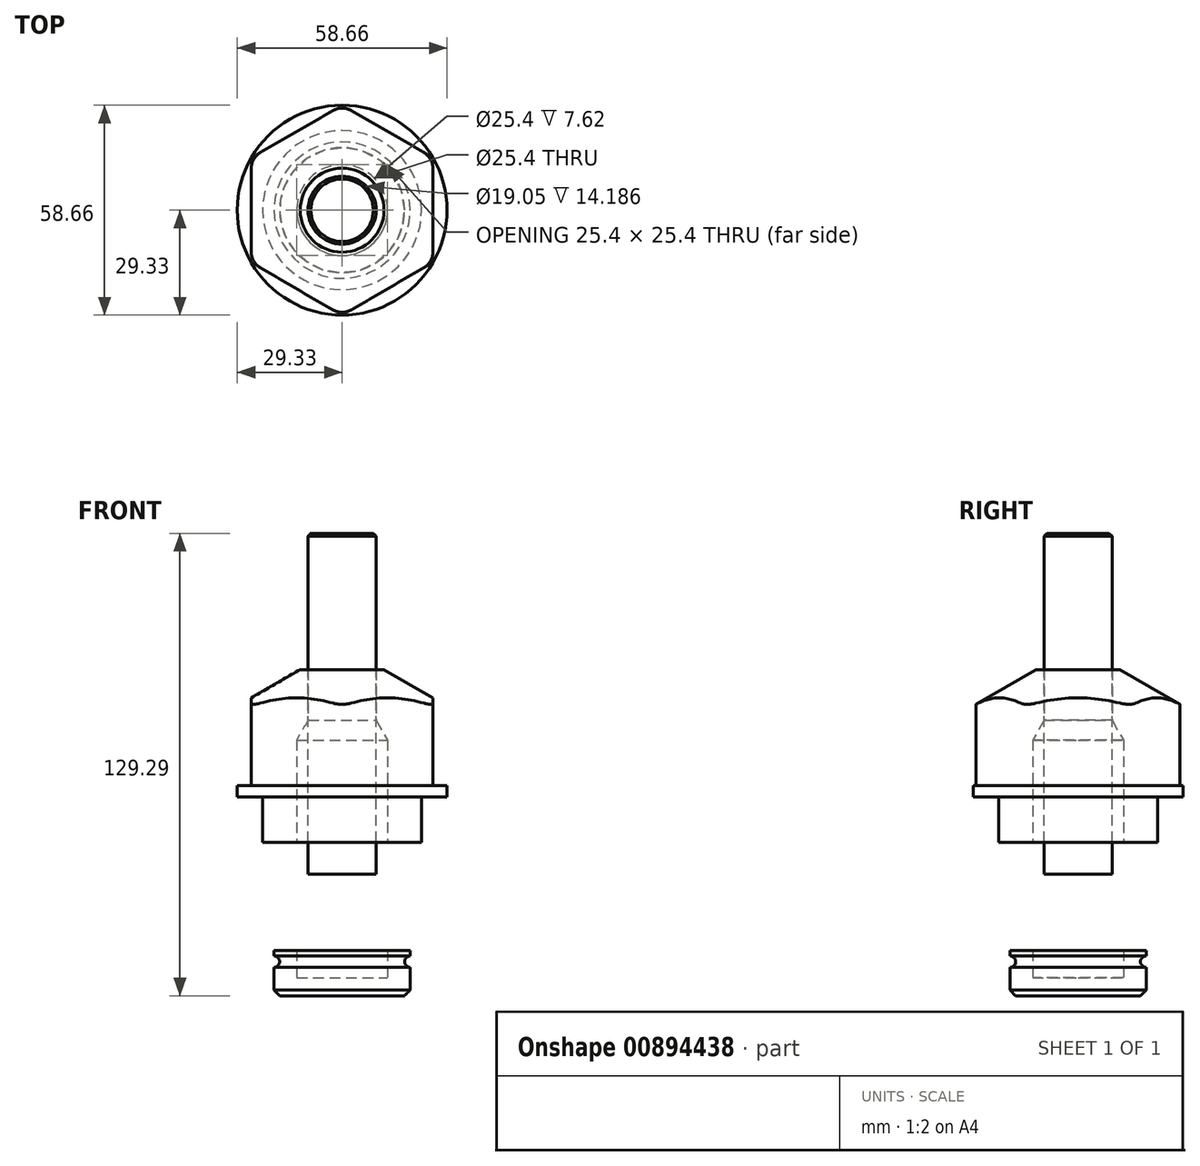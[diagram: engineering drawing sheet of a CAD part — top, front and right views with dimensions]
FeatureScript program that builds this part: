
annotation { "Feature Type Name" : "Feature", "Feature Type Description" : "" }
export const myFeature = defineFeature(function(context is Context, id is Id, definition is map)
    precondition{}
    {
        {
            var Q0;
            Q0=qCreatedBy(makeId("Top.planeOp"),FACE);
            var sketch = newSketch(context, id + "F0", { "sketchPlane" : qUnion([Q0])});
            skCircle(sketch, "E0", {"center": v(0, 0) * mm, "radius": 29.33 * mm});
            skLineSegment(sketch, "E1", {"start": v(0, 29.33) * mm, "end": v(0, -29.33) * mm, "construction": true});
            skLineSegment(sketch, "E2", {"start": v(-25.4, 14.66) * mm, "end": v(25.4, -14.66) * mm, "construction": true});
            skLineSegment(sketch, "E3", {"start": v(-25.4, -14.66) * mm, "end": v(25.4, 14.66) * mm, "construction": true});
            skLineSegment(sketch, "E4", {"start": v(-25.4, 14.66) * mm, "end": v(0, 29.33) * mm});
            skLineSegment(sketch, "E5", {"start": v(0, 29.33) * mm, "end": v(25.4, 14.66) * mm});
            skLineSegment(sketch, "E6", {"start": v(25.4, 14.66) * mm, "end": v(25.4, -14.66) * mm});
            skLineSegment(sketch, "E7", {"start": v(25.4, -14.66) * mm, "end": v(0, -29.33) * mm});
            skLineSegment(sketch, "E8", {"start": v(0, -29.33) * mm, "end": v(-25.4, -14.66) * mm});
            skLineSegment(sketch, "E9", {"start": v(-25.4, -14.66) * mm, "end": v(-25.4, 14.66) * mm});
            skCircle(sketch, "E10", {"center": v(0, 0) * mm, "radius": 7.94 * mm});
            skSolve(sketch);
        }
        {
            var Q0;
            Q0=makeQuery(id+"F0.imprint","IMPRINT",FACE,{"disambiguationData":[TD([[makeQuery(id+"F0.imprint","IMPRINT",EDGE,{"derivedFrom":sQuery(id+"F0.wireOp",EDGE,"E10")}),1.0]])]});
            var Q1;
            Q1=makeQuery(id+"F0.imprint","IMPRINT",FACE,{"disambiguationData":[TD([[makeQuery(id+"F0.imprint","IMPRINT",EDGE,{"derivedFrom":sQuery(id+"F0.wireOp",EDGE,"E4")}),-1.0]])]});
            extrude(context, id + "F1", {"entities" : qUnion([Q0, Q1]), "depth" : 35.56 * mm});
        }
        {
            var Q0;
            {var subQ0=sQuery(id+"F0.wireOp",EDGE,"E8");Q0=makeQuery(id+"F0.imprint","IMPRINT",FACE,{"disambiguationData":[TD([[makeQuery(id+"F0.imprint","IMPRINT",EDGE,{"derivedFrom":subQ0}),1.0]])]});}
            var Q1;
            {var subQ0=sQuery(id+"F0.wireOp",EDGE,"E7");Q1=makeQuery(id+"F0.imprint","IMPRINT",FACE,{"disambiguationData":[TD([[makeQuery(id+"F0.imprint","IMPRINT",EDGE,{"derivedFrom":subQ0}),1.0]])]});}
            var Q2;
            {var subQ0=sQuery(id+"F0.wireOp",EDGE,"E6");Q2=makeQuery(id+"F0.imprint","IMPRINT",FACE,{"disambiguationData":[TD([[makeQuery(id+"F0.imprint","IMPRINT",EDGE,{"derivedFrom":subQ0}),1.0]])]});}
            var Q3;
            Q3=makeQuery(id+"F0.imprint","IMPRINT",FACE,{"disambiguationData":[TD([[makeQuery(id+"F0.imprint","IMPRINT",EDGE,{"derivedFrom":sQuery(id+"F0.wireOp",EDGE,"E4")}),-1.0]])]});
            var Q4;
            {var subQ0=sQuery(id+"F0.wireOp",EDGE,"E5");Q4=makeQuery(id+"F0.imprint","IMPRINT",FACE,{"disambiguationData":[TD([[makeQuery(id+"F0.imprint","IMPRINT",EDGE,{"derivedFrom":subQ0}),1.0]])]});}
            var Q5;
            {var subQ0=sQuery(id+"F0.wireOp",EDGE,"E4");Q5=makeQuery(id+"F0.imprint","IMPRINT",FACE,{"disambiguationData":[TD([[makeQuery(id+"F0.imprint","IMPRINT",EDGE,{"derivedFrom":subQ0}),1.0]])]});}
            var Q6;
            {var subQ0=sQuery(id+"F0.wireOp",EDGE,"E9");Q6=makeQuery(id+"F0.imprint","IMPRINT",FACE,{"disambiguationData":[TD([[makeQuery(id+"F0.imprint","IMPRINT",EDGE,{"derivedFrom":subQ0}),1.0]])]});}
            extrude(context, id + "F2", {"entities" : qUnion([Q0, Q1, Q2, Q3, Q4, Q5, Q6]), "operationType" : NewBodyOperationType.ADD, "depth" : 3.17 * mm});
        }
        {
            var Q0;
            Q0=makeQuery(id+"F1.opExtrude","SWEPT_EDGE",EDGE,{"disambiguationData":[OSD([sQuery(id+"F0.wireOp",EDGE,"E0"),sQuery(id+"F0.wireOp",EDGE,"E7"),sQuery(id+"F0.wireOp",EDGE,"E8")])]});
            var Q1;
            Q1=makeQuery(id+"F1.opExtrude","SWEPT_EDGE",EDGE,{"disambiguationData":[OSD([sQuery(id+"F0.wireOp",EDGE,"E0"),sQuery(id+"F0.wireOp",EDGE,"E6"),sQuery(id+"F0.wireOp",EDGE,"E7")])]});
            var Q2;
            Q2=makeQuery(id+"F1.opExtrude","SWEPT_EDGE",EDGE,{"disambiguationData":[OSD([sQuery(id+"F0.wireOp",EDGE,"E0"),sQuery(id+"F0.wireOp",EDGE,"E5"),sQuery(id+"F0.wireOp",EDGE,"E6")])]});
            var Q3;
            Q3=makeQuery(id+"F1.opExtrude","SWEPT_EDGE",EDGE,{"disambiguationData":[OSD([sQuery(id+"F0.wireOp",EDGE,"E0"),sQuery(id+"F0.wireOp",EDGE,"E4"),sQuery(id+"F0.wireOp",EDGE,"E5")])]});
            var Q4;
            Q4=makeQuery(id+"F1.opExtrude","SWEPT_EDGE",EDGE,{"disambiguationData":[OSD([sQuery(id+"F0.wireOp",EDGE,"E0"),sQuery(id+"F0.wireOp",EDGE,"E4"),sQuery(id+"F0.wireOp",EDGE,"E9")])]});
            var Q5;
            Q5=makeQuery(id+"F1.opExtrude","SWEPT_EDGE",EDGE,{"disambiguationData":[OSD([sQuery(id+"F0.wireOp",EDGE,"E0"),sQuery(id+"F0.wireOp",EDGE,"E8"),sQuery(id+"F0.wireOp",EDGE,"E9")])]});
            fillet(context, id + "F3", {"entities" : qUnion([Q0, Q1, Q2, Q3, Q4, Q5]), "radius" : 5.08 * mm, "tangentPropagation" : true, "allowEdgeOverflow" : false});
        }
        {
            var Q0;
            Q0=qCreatedBy(makeId("Right.planeOp"),FACE);
            var sketch = newSketch(context, id + "F4", { "sketchPlane" : qUnion([Q0])});
            skLineSegment(sketch, "E11", {"start": v(0, 52) * mm, "end": v(0, 0) * mm, "construction": true});
            skLineSegment(sketch, "E12", {"start": v(11.73, 35.56) * mm, "end": v(35.4, 21.9) * mm});
            skLineSegment(sketch, "E13", {"start": v(35.4, 21.9) * mm, "end": v(35.4, 35.56) * mm});
            skLineSegment(sketch, "E14", {"start": v(35.4, 35.56) * mm, "end": v(11.73, 35.56) * mm});
            skLineSegment(sketch, "E15.0", {"start": v(11.73, 35.56) * mm, "end": v(-11.73, 35.56) * mm});
            skLineSegment(sketch, "E16.bottom", {"start": v(0, 0) * mm, "end": v(22.23, 0) * mm});
            skLineSegment(sketch, "E16.top", {"start": v(0, -12.7) * mm, "end": v(22.23, -12.7) * mm});
            skLineSegment(sketch, "E16.left", {"start": v(0, 0) * mm, "end": v(0, -12.7) * mm});
            skLineSegment(sketch, "E16.right", {"start": v(22.23, 0) * mm, "end": v(22.23, -12.7) * mm});
            skLineSegment(sketch, "E17.bottom", {"start": v(0, -12.7) * mm, "end": v(19.05, -12.7) * mm});
            skLineSegment(sketch, "E17.top", {"start": v(0, -27.69) * mm, "end": v(19.05, -27.69) * mm});
            skLineSegment(sketch, "E17.left", {"start": v(0, -12.7) * mm, "end": v(0, -27.69) * mm});
            skLineSegment(sketch, "E17.right", {"start": v(19.05, -12.7) * mm, "end": v(19.05, -27.69) * mm});
            skLineSegment(sketch, "E18.bottom", {"start": v(17.78, -27.69) * mm, "end": v(0, -27.69) * mm});
            skLineSegment(sketch, "E18.top", {"start": v(17.78, -42.93) * mm, "end": v(0, -42.93) * mm});
            skLineSegment(sketch, "E18.left", {"start": v(17.78, -27.69) * mm, "end": v(17.78, -42.93) * mm});
            skLineSegment(sketch, "E18.right", {"start": v(0, -27.69) * mm, "end": v(0, -42.93) * mm});
            skLineSegment(sketch, "E19.bottom", {"start": v(0, -42.93) * mm, "end": v(19.05, -42.93) * mm});
            skLineSegment(sketch, "E19.top", {"start": v(0, -55.63) * mm, "end": v(19.05, -55.63) * mm});
            skLineSegment(sketch, "E19.left", {"start": v(0, -42.93) * mm, "end": v(0, -55.63) * mm});
            skLineSegment(sketch, "E19.right", {"start": v(19.05, -42.93) * mm, "end": v(19.05, -55.63) * mm});
            skCircle(sketch, "E20", {"center": v(19.05, -24.51) * mm, "radius": 1.59 * mm});
            skCircle(sketch, "E21", {"center": v(19.05, -46.1) * mm, "radius": 1.59 * mm});
            skCircle(sketch, "E22", {"center": v(0, -17.46) * mm, "radius": 3.18 * mm});
            skCircle(sketch, "E23", {"center": v(0, -35.3) * mm, "radius": 3.18 * mm});
            skSolve(sketch);
        }
        {
            var Q0;
            Q0=makeQuery(id+"F4.imprint","IMPRINT",FACE,{"disambiguationData":[TD([[makeQuery(id+"F4.imprint","IMPRINT",EDGE,{"derivedFrom":sQuery(id+"F4.wireOp",EDGE,"E12")}),1.0]])]});
            var Q1;
            Q1=sQuery(id+"F4.wireOp",EDGE,"E11");
            revolve(context, id + "F5", {"operationType" : NewBodyOperationType.REMOVE, "entities" : qUnion([Q0]), "axis" : qUnion([Q1]), "revolveType" : RevolveType.FULL, "oppositeDirection" : true});
        }
        {
            var Q0;
            {var subQ7=sQuery(id+"F4.wireOp",EDGE,"E18.bottom");Q0=makeQuery(id+"F4.imprint","IMPRINT",FACE,{"disambiguationData":[TD([[makeQuery(id+"F4.imprint","IMPRINT",EDGE,{"derivedFrom":subQ7}),1.0]])]});}
            var Q1;
            {var subQ10=sQuery(id+"F4.wireOp",EDGE,"E17.bottom");Q1=makeQuery(id+"F4.imprint","IMPRINT",FACE,{"disambiguationData":[TD([[makeQuery(id+"F4.imprint","IMPRINT",EDGE,{"derivedFrom":subQ10}),-1.0]])]});}
            var Q2;
            Q2=makeQuery(id+"F4.imprint","IMPRINT",FACE,{"disambiguationData":[TD([[makeQuery(id+"F4.imprint","IMPRINT",EDGE,{"derivedFrom":sQuery(id+"F4.wireOp",EDGE,"E16.bottom")}),-1.0]])]});
            var Q3;
            {var subQ4=sQuery(id+"F4.wireOp",EDGE,"E19.top");Q3=makeQuery(id+"F4.imprint","IMPRINT",FACE,{"disambiguationData":[TD([[makeQuery(id+"F4.imprint","IMPRINT",EDGE,{"derivedFrom":subQ4}),1.0]])]});}
            var Q4;
            Q4=sQuery(id+"F4.wireOp",EDGE,"E11");
            revolve(context, id + "F6", {"operationType" : NewBodyOperationType.ADD, "entities" : qUnion([Q0, Q1, Q2, Q3]), "axis" : qUnion([Q4]), "revolveType" : RevolveType.FULL});
        }
        {
            var Q0;
            Q0=makeQuery(id+"F6.opRevolve","SWEPT_EDGE",EDGE,{"disambiguationData":[OSD([sQuery(id+"F4.wireOp",EDGE,"E19.top"),sQuery(id+"F4.wireOp",EDGE,"E19.right")])]});
            chamfer(context, id + "F7", {"entities" : qUnion([Q0]), "width" : 1.59 * mm, "tangentPropagation" : true});
        }
        {
            var Q0;
            {var subQ0=sQuery(id+"F4.wireOp",EDGE,"E16.right");var subQ1=sQuery(id+"F4.wireOp",EDGE,"E20");var subQ3=makeQuery(id+"F4.imprint","INTERSECT",VERTEX,{"disambiguationData":[OD(0.0)],"derivedFrom":[subQ0,subQ1]});Q0=makeQuery(id+"F4.imprint","IMPRINT",FACE,{"disambiguationData":[TD([[makeQuery(id+"F4.imprint","SKETCH_ENTITY",EDGE,{"disambiguationData":[TD([[subQ3,-1.0]])],"sketchEntityId":"E16.right"}),1.0]])]});}
            var Q1;
            {var subQ0=sQuery(id+"F4.wireOp",EDGE,"E20");var subQ1=sQuery(id+"F4.wireOp",EDGE,"E17.right");var subQ3=makeQuery(id+"F4.imprint","INTERSECT",VERTEX,{"disambiguationData":[OD(0.0)],"derivedFrom":[subQ1,subQ0]});Q1=makeQuery(id+"F4.imprint","IMPRINT",FACE,{"disambiguationData":[TD([[makeQuery(id+"F4.imprint","IMPRINT",EDGE,{"disambiguationData":[TD([[subQ3,-1.0]])],"derivedFrom":subQ1}),-1.0]])]});}
            var Q2;
            {var subQ0=sQuery(id+"F4.wireOp",EDGE,"E20");var subQ1=sQuery(id+"F4.wireOp",EDGE,"E17.right");var subQ3=makeQuery(id+"F4.imprint","INTERSECT",VERTEX,{"disambiguationData":[OD(0.0)],"derivedFrom":[subQ1,subQ0]});Q2=makeQuery(id+"F4.imprint","IMPRINT",FACE,{"disambiguationData":[TD([[makeQuery(id+"F4.imprint","IMPRINT",EDGE,{"disambiguationData":[TD([[subQ3,-1.0]])],"derivedFrom":subQ1}),1.0]])]});}
            var Q3;
            Q3=sQuery(id+"F4.wireOp",EDGE,"E11");
            revolve(context, id + "F8", {"entities" : qUnion([Q0, Q1, Q2]), "axis" : qUnion([Q3]), "revolveType" : RevolveType.FULL});
        }
        {
            var Q0;
            {var subQ0=sQuery(id+"F4.wireOp",EDGE,"E22");var subQ1=sQuery(id+"F4.wireOp",EDGE,"E17.left");var subQ3=makeQuery(id+"F4.imprint","INTERSECT",VERTEX,{"disambiguationData":[OD(0.0)],"derivedFrom":[subQ1,subQ0]});Q0=makeQuery(id+"F4.imprint","IMPRINT",FACE,{"disambiguationData":[TD([[makeQuery(id+"F4.imprint","IMPRINT",EDGE,{"disambiguationData":[TD([[subQ3,-1.0]])],"derivedFrom":subQ1}),-1.0]])]});}
            var Q1;
            {var subQ0=sQuery(id+"F4.wireOp",EDGE,"E22");var subQ1=sQuery(id+"F4.wireOp",EDGE,"E17.left");var subQ3=makeQuery(id+"F4.imprint","INTERSECT",VERTEX,{"disambiguationData":[OD(0.0)],"derivedFrom":[subQ1,subQ0]});Q1=makeQuery(id+"F4.imprint","IMPRINT",FACE,{"disambiguationData":[TD([[makeQuery(id+"F4.imprint","IMPRINT",EDGE,{"disambiguationData":[TD([[subQ3,-1.0]])],"derivedFrom":subQ1}),1.0]])]});}
            var Q2;
            {var subQ0=sQuery(id+"F4.wireOp",EDGE,"E23");var subQ1=sQuery(id+"F4.wireOp",EDGE,"E18.right");var subQ3=makeQuery(id+"F4.imprint","INTERSECT",VERTEX,{"disambiguationData":[OD(0.0)],"derivedFrom":[subQ1,subQ0]});Q2=makeQuery(id+"F4.imprint","IMPRINT",FACE,{"disambiguationData":[TD([[makeQuery(id+"F4.imprint","IMPRINT",EDGE,{"disambiguationData":[TD([[subQ3,-1.0]])],"derivedFrom":subQ1}),-1.0]])]});}
            var Q3;
            {var subQ0=sQuery(id+"F4.wireOp",EDGE,"E23");var subQ1=sQuery(id+"F4.wireOp",EDGE,"E18.right");var subQ3=makeQuery(id+"F4.imprint","INTERSECT",VERTEX,{"disambiguationData":[OD(0.0)],"derivedFrom":[subQ1,subQ0]});Q3=makeQuery(id+"F4.imprint","IMPRINT",FACE,{"disambiguationData":[TD([[makeQuery(id+"F4.imprint","IMPRINT",EDGE,{"disambiguationData":[TD([[subQ3,-1.0]])],"derivedFrom":subQ1}),1.0]])]});}
            extrude(context, id + "F9", {"entities" : qUnion([Q0, Q1, Q2, Q3]), "operationType" : NewBodyOperationType.REMOVE, "endBound" : BoundingType.THROUGH_ALL, "depth" : 25.4 * mm});
        }
        {
            var Q0;
            Q0=qCreatedBy(makeId("Right.planeOp"),FACE);
            var sketch = newSketch(context, id + "F10", { "sketchPlane" : qUnion([Q0])});
            skLineSegment(sketch, "E24", {"start": v(0, 73.66) * mm, "end": v(0, -50.55) * mm});
            skLineSegment(sketch, "E25", {"start": v(0, -50.55) * mm, "end": v(12.7, -50.55) * mm});
            skLineSegment(sketch, "E26", {"start": v(12.7, -50.55) * mm, "end": v(12.7, 15.88) * mm});
            skLineSegment(sketch, "E27", {"start": v(12.7, 15.88) * mm, "end": v(0, 15.88) * mm});
            skLineSegment(sketch, "E28", {"start": v(9.53, -21.6) * mm, "end": v(9.53, 73.66) * mm});
            skLineSegment(sketch, "E29", {"start": v(9.52, 73.66) * mm, "end": v(0, 73.66) * mm});
            skLineSegment(sketch, "E30", {"start": v(9.53, 21.37) * mm, "end": v(12.7, 15.88) * mm});
            skLineSegment(sketch, "E31.rect.bottom", {"start": v(12.7, -27.94) * mm, "end": v(-12.7, -27.94) * mm});
            skLineSegment(sketch, "E31.rect.top", {"start": v(12.7, -21.59) * mm, "end": v(-12.7, -21.59) * mm});
            skLineSegment(sketch, "E31.rect.left", {"start": v(12.7, -27.94) * mm, "end": v(12.7, -21.59) * mm});
            skLineSegment(sketch, "E31.rect.right", {"start": v(-12.7, -27.94) * mm, "end": v(-12.7, -21.59) * mm});
            skPoint(sketch, "E31.rect.middle", {"position": v(0, -24.77) * mm});
            skSolve(sketch);
        }
        {
            var Q0;
            {var subQ0=sQuery(id+"F10.wireOp",EDGE,"E29");Q0=makeQuery(id+"F10.imprint","IMPRINT",FACE,{"disambiguationData":[TD([[makeQuery(id+"F10.imprint","IMPRINT",EDGE,{"derivedFrom":subQ0}),1.0]])]});}
            var Q1;
            {var subQ0=sQuery(id+"F10.wireOp",EDGE,"E30");Q1=makeQuery(id+"F10.imprint","IMPRINT",FACE,{"disambiguationData":[TD([[makeQuery(id+"F10.imprint","IMPRINT",EDGE,{"derivedFrom":subQ0}),-1.0]])]});}
            var Q2;
            {var subQ1=sQuery(id+"F10.wireOp",EDGE,"E24");var subQ5=sQuery(id+"F10.wireOp",EDGE,"E27");var subQ7=makeQuery(id+"F10.imprint","INTERSECT",VERTEX,{"derivedFrom":[subQ1,subQ5]});Q2=makeQuery(id+"F10.imprint","IMPRINT",FACE,{"disambiguationData":[TD([[makeQuery(id+"F10.imprint","IMPRINT",EDGE,{"disambiguationData":[TD([[subQ7,-1.0]])],"derivedFrom":subQ1}),1.0]])]});}
            var Q3;
            {var subQ0=sQuery(id+"F10.wireOp",EDGE,"E31.rect.top");var subQ3=sQuery(id+"F10.wireOp",EDGE,"E28");var subQ4=makeQuery(id+"F10.imprint","INTERSECT",VERTEX,{"derivedFrom":[subQ3,subQ0]});Q3=makeQuery(id+"F10.imprint","IMPRINT",FACE,{"disambiguationData":[TD([[makeQuery(id+"F10.imprint","IMPRINT",EDGE,{"disambiguationData":[TD([[subQ4,-1.0]])],"derivedFrom":subQ3}),-1.0]])]});}
            var Q4;
            {var subQ5=sQuery(id+"F10.wireOp",EDGE,"E25");Q4=makeQuery(id+"F10.imprint","IMPRINT",FACE,{"disambiguationData":[TD([[makeQuery(id+"F10.imprint","IMPRINT",EDGE,{"derivedFrom":subQ5}),1.0]])]});}
            var Q5;
            {var subQ0=sQuery(id+"F10.wireOp",EDGE,"E31.rect.left");Q5=makeQuery(id+"F10.imprint","IMPRINT",FACE,{"disambiguationData":[TD([[makeQuery(id+"F10.imprint","IMPRINT",EDGE,{"derivedFrom":subQ0}),1.0]])]});}
            var Q6;
            Q6=sQuery(id+"F10.wireOp",EDGE,"E24");
            revolve(context, id + "F11", {"operationType" : NewBodyOperationType.REMOVE, "entities" : qUnion([Q0, Q1, Q2, Q3, Q4, Q5]), "axis" : qUnion([Q6]), "revolveType" : RevolveType.FULL, "oppositeDirection" : true});
        }
        {
            var Q0;
            {var subQ0=sQuery(id+"F10.wireOp",EDGE,"E29");Q0=makeQuery(id+"F10.imprint","IMPRINT",FACE,{"disambiguationData":[TD([[makeQuery(id+"F10.imprint","IMPRINT",EDGE,{"derivedFrom":subQ0}),1.0]])]});}
            var Q1;
            {var subQ1=sQuery(id+"F10.wireOp",EDGE,"E24");var subQ5=sQuery(id+"F10.wireOp",EDGE,"E27");var subQ7=makeQuery(id+"F10.imprint","INTERSECT",VERTEX,{"derivedFrom":[subQ1,subQ5]});Q1=makeQuery(id+"F10.imprint","IMPRINT",FACE,{"disambiguationData":[TD([[makeQuery(id+"F10.imprint","IMPRINT",EDGE,{"disambiguationData":[TD([[subQ7,-1.0]])],"derivedFrom":subQ1}),1.0]])]});}
            var Q2;
            {var subQ0=sQuery(id+"F10.wireOp",EDGE,"E31.rect.left");Q2=makeQuery(id+"F10.imprint","IMPRINT",FACE,{"disambiguationData":[TD([[makeQuery(id+"F10.imprint","IMPRINT",EDGE,{"derivedFrom":subQ0}),1.0]])]});}
            var Q3;
            Q3=sQuery(id+"F10.wireOp",EDGE,"E24");
            revolve(context, id + "F12", {"entities" : qUnion([Q0, Q1, Q2]), "axis" : qUnion([Q3]), "revolveType" : RevolveType.FULL});
        }
        {
            var Q0;
            Q0=makeQuery(id+"F12.opRevolve","SWEPT_EDGE",EDGE,{"disambiguationData":[OSD([sQuery(id+"F10.wireOp",EDGE,"E28"),sQuery(id+"F10.wireOp",EDGE,"E29")])]});
            chamfer(context, id + "F13", {"entities" : qUnion([Q0]), "width" : 0.8 * mm, "tangentPropagation" : true});
        }
        {
            var Q0;
            Q0=makeQuery(id+"F8.opRevolve","SWEPT_BODY",BODY,{"disambiguationData":[OSD([sQuery(id+"F4.wireOp",EDGE,"E20")])]});
            transform(context, id + "F14", {"entities" : qUnion([Q0]), "transformType" : TransformType.COPY});
        }
    });
